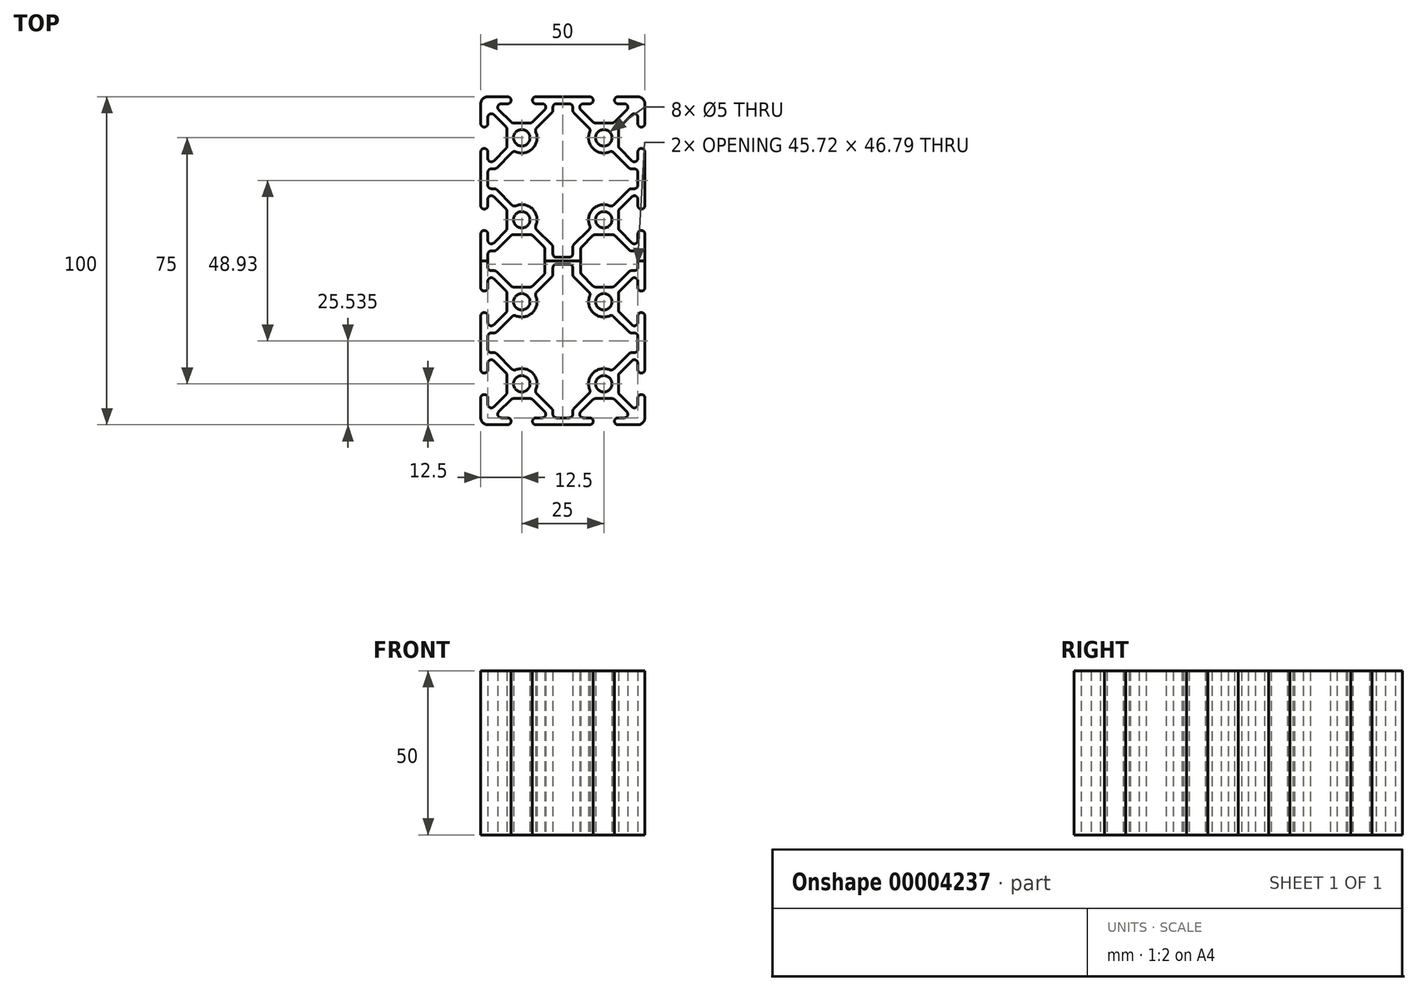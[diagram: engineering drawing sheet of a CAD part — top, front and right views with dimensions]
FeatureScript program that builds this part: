
annotation { "Feature Type Name" : "Feature", "Feature Type Description" : "" }
export const myFeature = defineFeature(function(context is Context, id is Id, definition is map)
    precondition{}
    {
        {
            var Q0;
            Q0=qCreatedBy(makeId("Top.planeOp"),FACE);
            var sketch = newSketch(context, id + "F0", { "sketchPlane" : qUnion([Q0])});
            skLineSegment(sketch, "E0", {"start": v(-12.5, 12.5) * mm, "end": v(-25, 25) * mm, "construction": true});
            skLineSegment(sketch, "E1", {"start": v(-25, 22.86) * mm, "end": v(-25, 16.82) * mm});
            skLineSegment(sketch, "E2", {"start": v(-22.86, 25) * mm, "end": v(-16.82, 25) * mm});
            skLineSegment(sketch, "E3", {"start": v(-16.82, 22.86) * mm, "end": v(-18.76, 22.86) * mm});
            skLineSegment(sketch, "E4", {"start": v(-22.86, 18.76) * mm, "end": v(-22.86, 16.82) * mm});
            skArc(sketch, "E5", {"start": v(-16.82, 25) * mm, "mid": v(-15.75, 23.93) * mm, "end": v(-16.82, 22.86) * mm});
            skArc(sketch, "E6", {"start": v(-22.86, 16.82) * mm, "mid": v(-23.93, 15.75) * mm, "end": v(-25, 16.82) * mm});
            skLineSegment(sketch, "E7", {"start": v(-19.52, 21.03) * mm, "end": v(-15.81, 17.32) * mm});
            skPoint(sketch, "E8.visualSharp", {"position": v(-25, 25) * mm});
            skLineSegment(sketch, "E8.filletArc", {"start": v(-25, 25) * mm, "end": v(-25, 25) * mm});
            skArc(sketch, "E9.filletArc", {"start": v(-21.03, 19.52) * mm, "mid": v(-22.2, 19.75) * mm, "end": v(-22.86, 18.76) * mm});
            skPoint(sketch, "E10.visualSharp", {"position": v(-21.35, 22.86) * mm});
            skArc(sketch, "E10.filletArc", {"start": v(-18.76, 22.86) * mm, "mid": v(-19.75, 22.2) * mm, "end": v(-19.52, 21.03) * mm});
            skArc(sketch, "E11.filletArc", {"start": v(-15.81, 17.32) * mm, "mid": v(-15.46, 17.1) * mm, "end": v(-15.05, 17.01) * mm});
            skCircle(sketch, "E12", {"center": v(-12.5, 12.5) * mm, "radius": 2.5 * mm});
            skLineSegment(sketch, "E13", {"start": v(0, 0) * mm, "end": v(0, 12.39) * mm, "construction": true});
            skCircle(sketch, "E14.0.MirrorC", {"center": v(12.5, 12.5) * mm, "radius": 2.5 * mm});
            skLineSegment(sketch, "E15", {"start": v(-12.5, 0) * mm, "end": v(-12.5, 12.5) * mm, "construction": true});
            skArc(sketch, "E16.0.MirrorCS", {"start": v(-9.19, 17.32) * mm, "mid": v(-9.54, 17.1) * mm, "end": v(-9.95, 17.01) * mm});
            skLineSegment(sketch, "E16.1.MirrorCS", {"start": v(-8.18, 22.86) * mm, "end": v(-6.24, 22.86) * mm});
            skLineSegment(sketch, "E16.3.MirrorCS", {"start": v(-5.48, 21.03) * mm, "end": v(-9.19, 17.32) * mm});
            skArc(sketch, "E16.8.MirrorCS", {"start": v(-8.18, 25) * mm, "mid": v(-9.25, 23.93) * mm, "end": v(-8.18, 22.86) * mm});
            skArc(sketch, "E16.11.MirrorCS", {"start": v(-6.24, 22.86) * mm, "mid": v(-5.25, 22.2) * mm, "end": v(-5.48, 21.03) * mm});
            skLineSegment(sketch, "E16.17.MirrorCS", {"start": v(0, 25) * mm, "end": v(-8.18, 25) * mm});
            skLineSegment(sketch, "E17", {"start": v(-15.05, 17.01) * mm, "end": v(-9.95, 17.01) * mm});
            skArc(sketch, "E18.1.MirrorCS", {"start": v(15.81, 17.32) * mm, "mid": v(15.46, 17.1) * mm, "end": v(15.05, 17.01) * mm});
            skArc(sketch, "E18.2.MirrorCS", {"start": v(9.19, 17.32) * mm, "mid": v(9.54, 17.1) * mm, "end": v(9.95, 17.01) * mm});
            skArc(sketch, "E18.3.MirrorCS", {"start": v(22.86, 16.82) * mm, "mid": v(23.93, 15.75) * mm, "end": v(25, 16.82) * mm});
            skLineSegment(sketch, "E18.5.MirrorCS", {"start": v(8.18, 22.86) * mm, "end": v(6.24, 22.86) * mm});
            skLineSegment(sketch, "E18.6.MirrorCS", {"start": v(19.52, 21.03) * mm, "end": v(15.81, 17.32) * mm});
            skLineSegment(sketch, "E18.7.MirrorCS", {"start": v(5.48, 21.03) * mm, "end": v(9.19, 17.32) * mm});
            skLineSegment(sketch, "E18.8.MirrorCS", {"start": v(12.5, 12.5) * mm, "end": v(25, 25) * mm, "construction": true});
            skArc(sketch, "E18.10.MirrorCS", {"start": v(16.82, 25) * mm, "mid": v(15.75, 23.93) * mm, "end": v(16.82, 22.86) * mm});
            skLineSegment(sketch, "E18.11.MirrorCS", {"start": v(15.05, 17.01) * mm, "end": v(9.95, 17.01) * mm});
            skPoint(sketch, "E18.12.MirrorP", {"position": v(21.35, 22.86) * mm});
            skLineSegment(sketch, "E18.14.MirrorCS", {"start": v(22.86, 25) * mm, "end": v(16.82, 25) * mm});
            skArc(sketch, "E18.15.MirrorCS", {"start": v(21.03, 19.52) * mm, "mid": v(22.2, 19.75) * mm, "end": v(22.86, 18.76) * mm});
            skPoint(sketch, "E18.16.MirrorP", {"position": v(25, 25) * mm});
            skLineSegment(sketch, "E18.17.MirrorCS", {"start": v(25, 22.86) * mm, "end": v(25, 16.82) * mm});
            skArc(sketch, "E18.18.MirrorCS", {"start": v(6.24, 22.86) * mm, "mid": v(5.25, 22.2) * mm, "end": v(5.48, 21.03) * mm});
            skArc(sketch, "E18.20.MirrorCS", {"start": v(18.76, 22.86) * mm, "mid": v(19.75, 22.2) * mm, "end": v(19.52, 21.03) * mm});
            skArc(sketch, "E18.21.MirrorCS", {"start": v(8.18, 25) * mm, "mid": v(9.25, 23.93) * mm, "end": v(8.18, 22.86) * mm});
            skLineSegment(sketch, "E18.22.MirrorCS", {"start": v(25, 25) * mm, "end": v(25, 25) * mm});
            skLineSegment(sketch, "E18.24.MirrorCS", {"start": v(22.86, 18.76) * mm, "end": v(22.86, 16.82) * mm});
            skLineSegment(sketch, "E18.25.MirrorCS", {"start": v(16.82, 22.86) * mm, "end": v(18.76, 22.86) * mm});
            skLineSegment(sketch, "E18.26.MirrorCS", {"start": v(0, 25) * mm, "end": v(8.18, 25) * mm});
            skLineSegment(sketch, "E19", {"start": v(-21.03, 19.52) * mm, "end": v(-17.32, 15.81) * mm});
            skLineSegment(sketch, "E20", {"start": v(0, 0) * mm, "end": v(-29.45, 0) * mm, "construction": true});
            skLineSegment(sketch, "E21", {"start": v(-17, 15.05) * mm, "end": v(-17, 12.5) * mm});
            skLineSegment(sketch, "E22", {"start": v(-12.5, 12.5) * mm, "end": v(-25, 12.5) * mm, "construction": true});
            skLineSegment(sketch, "E23.0.MirrorCS", {"start": v(21.03, 19.52) * mm, "end": v(17.32, 15.81) * mm});
            skLineSegment(sketch, "E24.0.MirrorCS", {"start": v(17, 15.05) * mm, "end": v(17, 12.5) * mm});
            skLineSegment(sketch, "E25.0.MirrorCS", {"start": v(-17, 9.95) * mm, "end": v(-17, 12.5) * mm});
            skLineSegment(sketch, "E26.0.MirrorCS", {"start": v(-21.03, 5.48) * mm, "end": v(-17.32, 9.19) * mm});
            skArc(sketch, "E27.0.MirrorCS", {"start": v(-21.03, 5.48) * mm, "mid": v(-22.2, 5.25) * mm, "end": v(-22.86, 6.24) * mm});
            skLineSegment(sketch, "E28.0.MirrorCS", {"start": v(-22.86, 6.24) * mm, "end": v(-22.86, 8.18) * mm});
            skArc(sketch, "E29.0.MirrorCS", {"start": v(-22.86, 8.18) * mm, "mid": v(-23.93, 9.25) * mm, "end": v(-25, 8.18) * mm});
            skLineSegment(sketch, "E30.0.MirrorCS", {"start": v(-25, 0) * mm, "end": v(-25, 8.18) * mm});
            skLineSegment(sketch, "E31.0.MirrorCS", {"start": v(17, 9.95) * mm, "end": v(17, 12.5) * mm});
            skLineSegment(sketch, "E32.0.MirrorCS", {"start": v(21.03, 5.48) * mm, "end": v(17.32, 9.19) * mm});
            skArc(sketch, "E33.0.MirrorCS", {"start": v(21.03, 5.48) * mm, "mid": v(22.2, 5.25) * mm, "end": v(22.86, 6.24) * mm});
            skLineSegment(sketch, "E34.0.MirrorCS", {"start": v(22.86, 6.24) * mm, "end": v(22.86, 8.18) * mm});
            skArc(sketch, "E35.0.MirrorCS", {"start": v(22.86, 8.18) * mm, "mid": v(23.93, 9.25) * mm, "end": v(25, 8.18) * mm});
            skLineSegment(sketch, "E36.0.MirrorCS", {"start": v(25, 0) * mm, "end": v(25, 8.18) * mm});
            skPoint(sketch, "E37.visualSharp", {"position": v(-17, 15.5) * mm});
            skArc(sketch, "E37.filletArc", {"start": v(-17, 15.05) * mm, "mid": v(-17.1, 15.46) * mm, "end": v(-17.32, 15.81) * mm});
            skPoint(sketch, "E38.visualSharp", {"position": v(-17, 9.5) * mm});
            skArc(sketch, "E38.filletArc", {"start": v(-17.32, 9.19) * mm, "mid": v(-17.1, 9.54) * mm, "end": v(-17, 9.95) * mm});
            skPoint(sketch, "E39.visualSharp", {"position": v(17, 9.5) * mm});
            skArc(sketch, "E39.filletArc", {"start": v(17, 9.95) * mm, "mid": v(17.1, 9.54) * mm, "end": v(17.32, 9.19) * mm});
            skPoint(sketch, "E40.visualSharp", {"position": v(17, 15.5) * mm});
            skArc(sketch, "E40.filletArc", {"start": v(17.32, 15.81) * mm, "mid": v(17.1, 15.46) * mm, "end": v(17, 15.05) * mm});
            skArc(sketch, "E41.1.MirrorCS", {"start": v(-17.32, -9.19) * mm, "mid": v(-17.1, -9.54) * mm, "end": v(-17, -9.95) * mm});
            skLineSegment(sketch, "E41.5.MirrorCS", {"start": v(-22.86, -6.24) * mm, "end": v(-22.86, -8.18) * mm});
            skLineSegment(sketch, "E41.8.MirrorCS", {"start": v(-12.5, 0) * mm, "end": v(-12.5, -12.5) * mm, "construction": true});
            skCircle(sketch, "E41.10.MirrorC", {"center": v(-12.5, -12.5) * mm, "radius": 2.5 * mm});
            skArc(sketch, "E41.12.MirrorCS", {"start": v(-21.03, -5.48) * mm, "mid": v(-22.2, -5.25) * mm, "end": v(-22.86, -6.24) * mm});
            skPoint(sketch, "E41.14.MirrorP", {"position": v(-17, -9.5) * mm});
            skLineSegment(sketch, "E41.15.MirrorCS", {"start": v(-21.03, -5.48) * mm, "end": v(-17.32, -9.19) * mm});
            skLineSegment(sketch, "E41.18.MirrorCS", {"start": v(-25, 0) * mm, "end": v(-25, -8.18) * mm});
            skArc(sketch, "E41.24.MirrorCS", {"start": v(-22.86, -8.18) * mm, "mid": v(-23.93, -9.25) * mm, "end": v(-25, -8.18) * mm});
            skLineSegment(sketch, "E41.29.MirrorCS", {"start": v(-12.5, -12.5) * mm, "end": v(-25, -12.5) * mm, "construction": true});
            skLineSegment(sketch, "E41.30.MirrorCS", {"start": v(-17, -9.95) * mm, "end": v(-17, -12.5) * mm});
            skArc(sketch, "E42.1.MirrorCS", {"start": v(17, -9.95) * mm, "mid": v(17.1, -9.54) * mm, "end": v(17.32, -9.19) * mm});
            skLineSegment(sketch, "E42.3.MirrorCS", {"start": v(22.86, -6.24) * mm, "end": v(22.86, -8.18) * mm});
            skArc(sketch, "E42.10.MirrorCS", {"start": v(21.03, -5.48) * mm, "mid": v(22.2, -5.25) * mm, "end": v(22.86, -6.24) * mm});
            skLineSegment(sketch, "E42.16.MirrorCS", {"start": v(17, -9.95) * mm, "end": v(17, -12.5) * mm});
            skArc(sketch, "E42.22.MirrorCS", {"start": v(22.86, -8.18) * mm, "mid": v(23.93, -9.25) * mm, "end": v(25, -8.18) * mm});
            skPoint(sketch, "E42.24.MirrorP", {"position": v(17, -9.5) * mm});
            skLineSegment(sketch, "E42.25.MirrorCS", {"start": v(21.03, -5.48) * mm, "end": v(17.32, -9.19) * mm});
            skCircle(sketch, "E42.27.MirrorC", {"center": v(12.5, -12.5) * mm, "radius": 2.5 * mm});
            skLineSegment(sketch, "E42.30.MirrorCS", {"start": v(25, 0) * mm, "end": v(25, -8.18) * mm});
            skArc(sketch, "E43.filletArc", {"start": v(-22.86, 25) * mm, "mid": v(-24.37, 24.37) * mm, "end": v(-25, 22.86) * mm});
            skArc(sketch, "E44.filletArc", {"start": v(25, 22.86) * mm, "mid": v(24.37, 24.37) * mm, "end": v(22.86, 25) * mm});
            skLineSegment(sketch, "E45", {"start": v(0, 22.86) * mm, "end": v(1.96, 22.86) * mm});
            skLineSegment(sketch, "E46", {"start": v(3.03, 21.8) * mm, "end": v(3.03, 20.9) * mm});
            skArc(sketch, "E47.0", {"start": v(14.31, 8.23) * mm, "mid": v(9.22, 9.22) * mm, "end": v(8.23, 14.31) * mm});
            skLineSegment(sketch, "E48.0", {"start": v(3.34, 20.15) * mm, "end": v(8, 15.49) * mm});
            skPoint(sketch, "E49.visualSharp", {"position": v(3.03, 22.86) * mm});
            skArc(sketch, "E49.filletArc", {"start": v(3.03, 21.8) * mm, "mid": v(2.71, 22.55) * mm, "end": v(1.96, 22.86) * mm});
            skPoint(sketch, "E50.visualSharp", {"position": v(8.55, 14.94) * mm});
            skArc(sketch, "E50.filletArc", {"start": v(8.23, 14.31) * mm, "mid": v(8.3, 14.93) * mm, "end": v(8, 15.49) * mm});
            skArc(sketch, "E51.0.MirrorCS", {"start": v(-14.31, 8.23) * mm, "mid": v(-9.22, 9.22) * mm, "end": v(-8.23, 14.31) * mm});
            skArc(sketch, "E52.0.MirrorCS", {"start": v(-8.23, 14.31) * mm, "mid": v(-8.3, 14.93) * mm, "end": v(-8, 15.49) * mm});
            skArc(sketch, "E53.0.MirrorCS", {"start": v(-3.03, 21.8) * mm, "mid": v(-2.71, 22.55) * mm, "end": v(-1.96, 22.86) * mm});
            skLineSegment(sketch, "E54.0.MirrorCS", {"start": v(0, 22.86) * mm, "end": v(-1.96, 22.86) * mm});
            skPoint(sketch, "E55.visualSharp", {"position": v(3.03, 20.46) * mm});
            skArc(sketch, "E55.filletArc", {"start": v(3.03, 20.9) * mm, "mid": v(3.1, 20.5) * mm, "end": v(3.34, 20.15) * mm});
            skLineSegment(sketch, "E56.0.MirrorCS", {"start": v(-3.34, 20.15) * mm, "end": v(-8, 15.49) * mm});
            skArc(sketch, "E57.0.MirrorCS", {"start": v(-3.03, 20.9) * mm, "mid": v(-3.1, 20.5) * mm, "end": v(-3.34, 20.15) * mm});
            skLineSegment(sketch, "E58.0.MirrorCS", {"start": v(-3.03, 21.8) * mm, "end": v(-3.03, 20.9) * mm});
            skPoint(sketch, "E59.visualSharp", {"position": v(-12.5, 7.86) * mm});
            skPoint(sketch, "E60.visualSharp", {"position": v(-12.5, -7.86) * mm});
            skPoint(sketch, "E61.visualSharp", {"position": v(12.5, -7.86) * mm});
            skArc(sketch, "E62.0.MirrorCS", {"start": v(-14.31, 8.23) * mm, "mid": v(-14.93, 8.3) * mm, "end": v(-15.49, 8) * mm});
            skLineSegment(sketch, "E63.0.MirrorCS", {"start": v(-20.15, 3.34) * mm, "end": v(-15.49, 8) * mm});
            skArc(sketch, "E64.0.MirrorCS", {"start": v(-20.9, 3.03) * mm, "mid": v(-20.5, 3.1) * mm, "end": v(-20.15, 3.34) * mm});
            skLineSegment(sketch, "E65.0.MirrorCS", {"start": v(-21.79, 3.03) * mm, "end": v(-20.9, 3.03) * mm});
            skArc(sketch, "E66.0.MirrorCS", {"start": v(-21.79, 3.03) * mm, "mid": v(-22.55, 2.71) * mm, "end": v(-22.86, 1.96) * mm});
            skLineSegment(sketch, "E67.0.MirrorCS", {"start": v(-22.86, 0) * mm, "end": v(-22.86, 1.96) * mm});
            skArc(sketch, "E68.0.MirrorCS", {"start": v(14.31, 8.23) * mm, "mid": v(14.93, 8.3) * mm, "end": v(15.49, 8) * mm});
            skArc(sketch, "E69.0.MirrorCS", {"start": v(-12.5, 7.86) * mm, "mid": v(-8.63, 9.94) * mm, "end": v(-8.23, 14.31) * mm});
            skLineSegment(sketch, "E70.0.MirrorCS", {"start": v(20.15, 3.34) * mm, "end": v(15.49, 8) * mm});
            skArc(sketch, "E71.0.MirrorCS", {"start": v(20.9, 3.03) * mm, "mid": v(20.5, 3.1) * mm, "end": v(20.15, 3.34) * mm});
            skLineSegment(sketch, "E72.0.MirrorCS", {"start": v(21.79, 3.03) * mm, "end": v(20.9, 3.03) * mm});
            skArc(sketch, "E73.0.MirrorCS", {"start": v(21.79, 3.03) * mm, "mid": v(22.55, 2.71) * mm, "end": v(22.86, 1.96) * mm});
            skLineSegment(sketch, "E74.0.MirrorCS", {"start": v(22.86, 0) * mm, "end": v(22.86, 1.96) * mm});
            skPoint(sketch, "E75.orphan", {"position": v(12.5, 7.86) * mm});
            skArc(sketch, "E76.0.MirrorCS", {"start": v(-20.9, -3.03) * mm, "mid": v(-20.5, -3.1) * mm, "end": v(-20.15, -3.34) * mm});
            skLineSegment(sketch, "E76.1.MirrorCS", {"start": v(-21.79, -3.03) * mm, "end": v(-20.9, -3.03) * mm});
            skArc(sketch, "E76.2.MirrorCS", {"start": v(-21.79, -3.03) * mm, "mid": v(-22.55, -2.71) * mm, "end": v(-22.86, -1.96) * mm});
            skLineSegment(sketch, "E76.3.MirrorCS", {"start": v(-22.86, 0) * mm, "end": v(-22.86, -1.96) * mm});
            skLineSegment(sketch, "E77.0.MirrorCS", {"start": v(-20.15, -3.34) * mm, "end": v(-15.49, -8) * mm});
            skArc(sketch, "E78.0.MirrorCS", {"start": v(-14.31, -8.23) * mm, "mid": v(-14.93, -8.3) * mm, "end": v(-15.49, -8) * mm});
            skArc(sketch, "E79.0.MirrorCS", {"start": v(-14.31, -8.23) * mm, "mid": v(-9.22, -9.22) * mm, "end": v(-8.23, -14.31) * mm});
            skArc(sketch, "E80.0.MirrorCS", {"start": v(14.31, -8.23) * mm, "mid": v(9.22, -9.22) * mm, "end": v(8.23, -14.31) * mm});
            skArc(sketch, "E81.0.MirrorCS", {"start": v(14.31, -8.23) * mm, "mid": v(14.93, -8.3) * mm, "end": v(15.49, -8) * mm});
            skLineSegment(sketch, "E82.0.MirrorCS", {"start": v(20.15, -3.34) * mm, "end": v(15.49, -8) * mm});
            skArc(sketch, "E83.0.MirrorCS", {"start": v(20.9, -3.03) * mm, "mid": v(20.5, -3.1) * mm, "end": v(20.15, -3.34) * mm});
            skLineSegment(sketch, "E84.0.MirrorCS", {"start": v(21.79, -3.03) * mm, "end": v(20.9, -3.03) * mm});
            skArc(sketch, "E85.0.MirrorCS", {"start": v(21.79, -3.03) * mm, "mid": v(22.55, -2.71) * mm, "end": v(22.86, -1.96) * mm});
            skLineSegment(sketch, "E86.0.MirrorCS", {"start": v(22.86, 0) * mm, "end": v(22.86, -1.96) * mm});
            skArc(sketch, "E87.1.MirrorCS", {"start": v(14.31, -33.23) * mm, "mid": v(14.93, -33.3) * mm, "end": v(15.49, -33) * mm});
            skLineSegment(sketch, "E87.2.MirrorCS", {"start": v(22.86, -25) * mm, "end": v(22.86, -23.04) * mm});
            skLineSegment(sketch, "E87.3.MirrorCS", {"start": v(21.79, -28.03) * mm, "end": v(20.9, -28.03) * mm});
            skLineSegment(sketch, "E87.4.MirrorCS", {"start": v(-22.86, -25) * mm, "end": v(-22.86, -23.04) * mm});
            skArc(sketch, "E87.5.MirrorCS", {"start": v(20.9, -28.03) * mm, "mid": v(20.5, -28.1) * mm, "end": v(20.15, -28.34) * mm});
            skArc(sketch, "E87.6.MirrorCS", {"start": v(21.79, -21.97) * mm, "mid": v(22.55, -22.29) * mm, "end": v(22.86, -23.04) * mm});
            skArc(sketch, "E87.7.MirrorCS", {"start": v(-21.79, -28.03) * mm, "mid": v(-22.55, -27.71) * mm, "end": v(-22.86, -26.96) * mm});
            skLineSegment(sketch, "E87.8.MirrorCS", {"start": v(-22.86, -18.76) * mm, "end": v(-22.86, -16.82) * mm});
            skArc(sketch, "E87.10.MirrorCS", {"start": v(-21.79, -21.97) * mm, "mid": v(-22.55, -22.29) * mm, "end": v(-22.86, -23.04) * mm});
            skLineSegment(sketch, "E87.12.MirrorCS", {"start": v(-21.79, -28.03) * mm, "end": v(-20.9, -28.03) * mm});
            skLineSegment(sketch, "E87.14.MirrorCS", {"start": v(-22.86, -31.24) * mm, "end": v(-22.86, -33.18) * mm});
            skArc(sketch, "E87.15.MirrorCS", {"start": v(17, -15.05) * mm, "mid": v(17.1, -15.46) * mm, "end": v(17.32, -15.81) * mm});
            skArc(sketch, "E87.16.MirrorCS", {"start": v(17, -34.95) * mm, "mid": v(17.1, -34.54) * mm, "end": v(17.32, -34.19) * mm});
            skLineSegment(sketch, "E87.17.MirrorCS", {"start": v(22.86, -25) * mm, "end": v(22.86, -26.96) * mm});
            skArc(sketch, "E87.18.MirrorCS", {"start": v(-20.9, -28.03) * mm, "mid": v(-20.5, -28.1) * mm, "end": v(-20.15, -28.34) * mm});
            skLineSegment(sketch, "E87.19.MirrorCS", {"start": v(22.86, -18.76) * mm, "end": v(22.86, -16.82) * mm});
            skArc(sketch, "E87.20.MirrorCS", {"start": v(20.9, -21.97) * mm, "mid": v(20.5, -21.9) * mm, "end": v(20.15, -21.66) * mm});
            skArc(sketch, "E87.21.MirrorCS", {"start": v(-17.32, -34.19) * mm, "mid": v(-17.1, -34.54) * mm, "end": v(-17.01, -34.95) * mm});
            skLineSegment(sketch, "E87.22.MirrorCS", {"start": v(22.86, -31.24) * mm, "end": v(22.86, -33.18) * mm});
            skLineSegment(sketch, "E87.23.MirrorCS", {"start": v(-22.86, -25) * mm, "end": v(-22.86, -26.96) * mm});
            skArc(sketch, "E87.24.MirrorCS", {"start": v(-20.9, -21.97) * mm, "mid": v(-20.5, -21.9) * mm, "end": v(-20.15, -21.66) * mm});
            skLineSegment(sketch, "E87.25.MirrorCS", {"start": v(21.79, -21.97) * mm, "end": v(20.9, -21.97) * mm});
            skLineSegment(sketch, "E87.26.MirrorCS", {"start": v(-21.79, -21.97) * mm, "end": v(-20.9, -21.97) * mm});
            skArc(sketch, "E87.27.MirrorCS", {"start": v(21.79, -28.03) * mm, "mid": v(22.55, -27.71) * mm, "end": v(22.86, -26.96) * mm});
            skArc(sketch, "E87.28.MirrorCS", {"start": v(-17.32, -15.81) * mm, "mid": v(-17.1, -15.46) * mm, "end": v(-17, -15.05) * mm});
            skLineSegment(sketch, "E87.29.MirrorCS", {"start": v(-25, -25) * mm, "end": v(-25, -33.18) * mm});
            skLineSegment(sketch, "E87.30.MirrorCS", {"start": v(17.01, -9.95) * mm, "end": v(17.01, -12.5) * mm});
            skLineSegment(sketch, "E87.31.MirrorCS", {"start": v(21.03, -19.52) * mm, "end": v(17.32, -15.81) * mm});
            skLineSegment(sketch, "E87.32.MirrorCS", {"start": v(-20.15, -28.34) * mm, "end": v(-15.81, -32.68) * mm});
            skPoint(sketch, "E87.33.MirrorP", {"position": v(-17, -15.5) * mm});
            skArc(sketch, "E87.35.MirrorCS", {"start": v(-22.86, -16.82) * mm, "mid": v(-23.93, -15.75) * mm, "end": v(-25, -16.82) * mm});
            skLineSegment(sketch, "E87.36.MirrorCS", {"start": v(-21.03, -30.48) * mm, "end": v(-17.32, -34.19) * mm});
            skLineSegment(sketch, "E87.37.MirrorCS", {"start": v(20.15, -21.66) * mm, "end": v(15.81, -17.32) * mm});
            skArc(sketch, "E87.38.MirrorCS", {"start": v(-21.03, -19.52) * mm, "mid": v(-22.2, -19.75) * mm, "end": v(-22.86, -18.76) * mm});
            skArc(sketch, "E87.39.MirrorCS", {"start": v(-22.86, -33.18) * mm, "mid": v(-23.93, -34.25) * mm, "end": v(-25, -33.18) * mm});
            skLineSegment(sketch, "E87.41.MirrorCS", {"start": v(0, -25) * mm, "end": v(-29.45, -25) * mm, "construction": true});
            skLineSegment(sketch, "E87.42.MirrorCS", {"start": v(-17, -15.05) * mm, "end": v(-17, -12.5) * mm});
            skArc(sketch, "E87.43.MirrorCS", {"start": v(22.86, -33.18) * mm, "mid": v(23.93, -34.25) * mm, "end": v(25, -33.18) * mm});
            skLineSegment(sketch, "E87.44.MirrorCS", {"start": v(17, -15.05) * mm, "end": v(17, -12.5) * mm});
            skLineSegment(sketch, "E87.46.MirrorCS", {"start": v(21.03, -30.48) * mm, "end": v(17.32, -34.19) * mm});
            skPoint(sketch, "E87.48.MirrorP", {"position": v(17, -15.5) * mm});
            skPoint(sketch, "E87.49.MirrorP", {"position": v(-17.01, -34.5) * mm});
            skPoint(sketch, "E87.50.MirrorP", {"position": v(-12.5, -17.14) * mm});
            skLineSegment(sketch, "E87.51.MirrorCS", {"start": v(25, -25) * mm, "end": v(25, -33.18) * mm});
            skLineSegment(sketch, "E87.52.MirrorCS", {"start": v(25, -25) * mm, "end": v(25, -16.82) * mm});
            skLineSegment(sketch, "E87.53.MirrorCS", {"start": v(17, -34.95) * mm, "end": v(17, -37.5) * mm});
            skArc(sketch, "E87.54.MirrorCS", {"start": v(21.03, -30.48) * mm, "mid": v(22.2, -30.25) * mm, "end": v(22.86, -31.24) * mm});
            skLineSegment(sketch, "E87.55.MirrorCS", {"start": v(-25, -25) * mm, "end": v(-25, -16.82) * mm});
            skLineSegment(sketch, "E87.57.MirrorCS", {"start": v(-20.15, -21.66) * mm, "end": v(-15.81, -17.32) * mm});
            skPoint(sketch, "E87.58.MirrorP", {"position": v(12.5, -32.86) * mm});
            skPoint(sketch, "E87.59.MirrorP", {"position": v(17, -34.5) * mm});
            skLineSegment(sketch, "E87.60.MirrorCS", {"start": v(-12.5, -37.5) * mm, "end": v(-25, -37.5) * mm, "construction": true});
            skArc(sketch, "E87.61.MirrorCS", {"start": v(21.03, -19.52) * mm, "mid": v(22.2, -19.75) * mm, "end": v(22.86, -18.76) * mm});
            skLineSegment(sketch, "E87.62.MirrorCS", {"start": v(0, -25) * mm, "end": v(0, -37.39) * mm, "construction": true});
            skLineSegment(sketch, "E87.64.MirrorCS", {"start": v(20.15, -28.34) * mm, "end": v(15.81, -32.68) * mm});
            skArc(sketch, "E87.65.MirrorCS", {"start": v(22.86, -16.82) * mm, "mid": v(23.93, -15.75) * mm, "end": v(25, -16.82) * mm});
            skLineSegment(sketch, "E87.66.MirrorCS", {"start": v(-17.01, -34.95) * mm, "end": v(-17.01, -37.5) * mm});
            skLineSegment(sketch, "E87.67.MirrorCS", {"start": v(-12.5, -25) * mm, "end": v(-12.5, -37.5) * mm, "construction": true});
            skArc(sketch, "E87.68.MirrorCS", {"start": v(-21.03, -30.48) * mm, "mid": v(-22.2, -30.25) * mm, "end": v(-22.86, -31.24) * mm});
            skLineSegment(sketch, "E87.69.MirrorCS", {"start": v(-12.5, -25) * mm, "end": v(-12.5, -12.5) * mm, "construction": true});
            skLineSegment(sketch, "E87.70.MirrorCS", {"start": v(-21.03, -19.52) * mm, "end": v(-17.32, -15.81) * mm});
            skLineSegment(sketch, "E88.0.MirrorCS", {"start": v(-3.34, -20.15) * mm, "end": v(-8, -15.49) * mm});
            skLineSegment(sketch, "E89.0.MirrorCS", {"start": v(-5.8, -20.72) * mm, "end": v(-9.19, -17.32) * mm});
            skArc(sketch, "E90.0.MirrorCS", {"start": v(-3.03, -20.9) * mm, "mid": v(-3.1, -20.5) * mm, "end": v(-3.34, -20.15) * mm});
            skLineSegment(sketch, "E91.0.MirrorCS", {"start": v(-3.03, -22.86) * mm, "end": v(-3.03, -20.9) * mm});
            skLineSegment(sketch, "E92.0.MirrorCS", {"start": v(3.34, -20.15) * mm, "end": v(8, -15.49) * mm});
            skArc(sketch, "E93.0.MirrorCS", {"start": v(3.03, -20.9) * mm, "mid": v(3.1, -20.5) * mm, "end": v(3.34, -20.15) * mm});
            skLineSegment(sketch, "E94.0.MirrorCS", {"start": v(3.03, -22.86) * mm, "end": v(3.03, -20.9) * mm});
            skPoint(sketch, "E95.newPointA", {"position": v(-8.23, -14.31) * mm});
            skPoint(sketch, "E95.newPointB", {"position": v(-8, -15.49) * mm});
            skArc(sketch, "E95.filletArc", {"start": v(-8.23, -14.31) * mm, "mid": v(-8.3, -14.93) * mm, "end": v(-8, -15.49) * mm});
            skPoint(sketch, "E96.newPointA", {"position": v(8.23, -14.31) * mm});
            skPoint(sketch, "E96.newPointB", {"position": v(8, -15.49) * mm});
            skArc(sketch, "E96.filletArc", {"start": v(8, -15.49) * mm, "mid": v(8.3, -14.93) * mm, "end": v(8.23, -14.31) * mm});
            skLineSegment(sketch, "E97.0.MirrorCS", {"start": v(-15.05, -17.01) * mm, "end": v(-9.95, -17.01) * mm});
            skPoint(sketch, "E98.newPointB", {"position": v(-15.05, -17.01) * mm});
            skArc(sketch, "E98.filletArc", {"start": v(-15.05, -17.01) * mm, "mid": v(-15.46, -17.1) * mm, "end": v(-15.81, -17.32) * mm});
            skPoint(sketch, "E99.visualSharp", {"position": v(-9.5, -17) * mm});
            skArc(sketch, "E99.filletArc", {"start": v(-9.19, -17.32) * mm, "mid": v(-9.54, -17.1) * mm, "end": v(-9.95, -17.01) * mm});
            skLineSegment(sketch, "E100.0.MirrorCS", {"start": v(-15.05, -32.99) * mm, "end": v(-9.95, -32.99) * mm});
            skLineSegment(sketch, "E101.0.MirrorCS", {"start": v(-5.8, -29.28) * mm, "end": v(-9.19, -32.68) * mm});
            skPoint(sketch, "E102.newPointB", {"position": v(-15.05, -32.99) * mm});
            skArc(sketch, "E102.filletArc", {"start": v(-15.81, -32.68) * mm, "mid": v(-15.46, -32.9) * mm, "end": v(-15.05, -32.99) * mm});
            skPoint(sketch, "E103.newPointA", {"position": v(-9.19, -32.68) * mm});
            skPoint(sketch, "E103.newPointB", {"position": v(-9.95, -32.99) * mm});
            skArc(sketch, "E103.filletArc", {"start": v(-9.95, -32.99) * mm, "mid": v(-9.54, -32.9) * mm, "end": v(-9.19, -32.68) * mm});
            skLineSegment(sketch, "E104", {"start": v(-5.48, -21.48) * mm, "end": v(-5.48, -28.52) * mm});
            skPoint(sketch, "E105.visualSharp", {"position": v(-5.48, -21.03) * mm});
            skArc(sketch, "E105.filletArc", {"start": v(-5.48, -21.48) * mm, "mid": v(-5.56, -21.07) * mm, "end": v(-5.8, -20.72) * mm});
            skPoint(sketch, "E106.visualSharp", {"position": v(-5.48, -28.97) * mm});
            skArc(sketch, "E106.filletArc", {"start": v(-5.8, -29.28) * mm, "mid": v(-5.56, -28.93) * mm, "end": v(-5.48, -28.52) * mm});
            skLineSegment(sketch, "E107", {"start": v(-1.96, -23.93) * mm, "end": v(1.96, -23.93) * mm});
            skPoint(sketch, "E108.orphan", {"position": v(-3.03, -21.8) * mm});
            skPoint(sketch, "E109.orphan", {"position": v(3.03, -21.8) * mm});
            skArc(sketch, "E110.filletArc", {"start": v(-3.03, -22.86) * mm, "mid": v(-2.71, -23.62) * mm, "end": v(-1.96, -23.93) * mm});
            skArc(sketch, "E111.filletArc", {"start": v(1.96, -23.93) * mm, "mid": v(2.71, -23.62) * mm, "end": v(3.03, -22.86) * mm});
            skLineSegment(sketch, "E112.0.MirrorCS", {"start": v(15.05, -17.01) * mm, "end": v(9.95, -17.01) * mm});
            skLineSegment(sketch, "E113.0.MirrorCS", {"start": v(5.8, -20.72) * mm, "end": v(9.19, -17.32) * mm});
            skLineSegment(sketch, "E114.0.MirrorCS", {"start": v(5.48, -21.48) * mm, "end": v(5.48, -28.52) * mm});
            skLineSegment(sketch, "E115.0.MirrorCS", {"start": v(5.8, -29.28) * mm, "end": v(9.19, -32.68) * mm});
            skLineSegment(sketch, "E116.0.MirrorCS", {"start": v(15.05, -33) * mm, "end": v(9.95, -33) * mm});
            skPoint(sketch, "E117.newPointA", {"position": v(9.19, -17.32) * mm});
            skPoint(sketch, "E117.newPointB", {"position": v(9.95, -17.01) * mm});
            skArc(sketch, "E117.filletArc", {"start": v(9.95, -17.01) * mm, "mid": v(9.54, -17.1) * mm, "end": v(9.19, -17.32) * mm});
            skPoint(sketch, "E118.newPointA", {"position": v(15.05, -17.01) * mm});
            skArc(sketch, "E118.filletArc", {"start": v(15.81, -17.32) * mm, "mid": v(15.46, -17.1) * mm, "end": v(15.05, -17.01) * mm});
            skPoint(sketch, "E119.newPointA", {"position": v(15.05, -33) * mm});
            skPoint(sketch, "E119.newPointB", {"position": v(15.49, -33) * mm});
            skArc(sketch, "E119.filletArc", {"start": v(15.05, -33) * mm, "mid": v(15.46, -32.9) * mm, "end": v(15.81, -32.68) * mm});
            skPoint(sketch, "E120.newPointA", {"position": v(5.8, -29.28) * mm});
            skPoint(sketch, "E120.newPointB", {"position": v(5.48, -28.52) * mm});
            skArc(sketch, "E120.filletArc", {"start": v(5.48, -28.52) * mm, "mid": v(5.56, -28.93) * mm, "end": v(5.8, -29.28) * mm});
            skPoint(sketch, "E121.newPointA", {"position": v(9.19, -32.68) * mm});
            skPoint(sketch, "E121.newPointB", {"position": v(9.95, -33) * mm});
            skArc(sketch, "E121.filletArc", {"start": v(9.19, -32.68) * mm, "mid": v(9.54, -32.9) * mm, "end": v(9.95, -33) * mm});
            skPoint(sketch, "E122.newPointA", {"position": v(5.8, -20.72) * mm});
            skPoint(sketch, "E122.newPointB", {"position": v(5.48, -21.48) * mm});
            skArc(sketch, "E122.filletArc", {"start": v(5.8, -20.72) * mm, "mid": v(5.56, -21.07) * mm, "end": v(5.48, -21.48) * mm});
            skLineSegment(sketch, "E123.0.MirrorCS", {"start": v(-17.01, -40.05) * mm, "end": v(-17.01, -37.5) * mm});
            skLineSegment(sketch, "E124", {"start": v(-25, -25) * mm, "end": v(25, -25) * mm});
            skSolve(sketch);
        }
        {
            var Q0;
            Q0=makeQuery(id+"F0.imprint","IMPRINT",FACE,{"disambiguationData":[TD([[makeQuery(id+"F0.imprint","IMPRINT",EDGE,{"derivedFrom":sQuery(id+"F0.wireOp",EDGE,"E1")}),1.0]])]});
            extrude(context, id + "F1", {"entities" : qUnion([Q0]), "depth" : 50 * mm});
        }
        {
            var Q0;
            Q0=makeQuery(id+"F1.opExtrude","SWEPT_BODY",BODY,{"disambiguationData":[OSD([sQuery(id+"F0.wireOp",EDGE,"E1"),sQuery(id+"F0.wireOp",EDGE,"E2"),sQuery(id+"F0.wireOp",EDGE,"E3"),sQuery(id+"F0.wireOp",EDGE,"E4"),sQuery(id+"F0.wireOp",EDGE,"E5"),sQuery(id+"F0.wireOp",EDGE,"E6"),sQuery(id+"F0.wireOp",EDGE,"E7"),sQuery(id+"F0.wireOp",EDGE,"E9.filletArc"),sQuery(id+"F0.wireOp",EDGE,"E10.filletArc"),sQuery(id+"F0.wireOp",EDGE,"E11.filletArc"),sQuery(id+"F0.wireOp",EDGE,"E12"),sQuery(id+"F0.wireOp",EDGE,"E14.0.MirrorC"),sQuery(id+"F0.wireOp",EDGE,"E16.0.MirrorCS"),sQuery(id+"F0.wireOp",EDGE,"E16.1.MirrorCS"),sQuery(id+"F0.wireOp",EDGE,"E16.3.MirrorCS"),sQuery(id+"F0.wireOp",EDGE,"E16.8.MirrorCS"),sQuery(id+"F0.wireOp",EDGE,"E16.11.MirrorCS"),sQuery(id+"F0.wireOp",EDGE,"E17"),sQuery(id+"F0.wireOp",EDGE,"E18.1.MirrorCS"),sQuery(id+"F0.wireOp",EDGE,"E18.2.MirrorCS"),sQuery(id+"F0.wireOp",EDGE,"E18.5.MirrorCS"),sQuery(id+"F0.wireOp",EDGE,"E18.6.MirrorCS"),sQuery(id+"F0.wireOp",EDGE,"E18.7.MirrorCS"),sQuery(id+"F0.wireOp",EDGE,"E18.10.MirrorCS"),sQuery(id+"F0.wireOp",EDGE,"E18.11.MirrorCS"),sQuery(id+"F0.wireOp",EDGE,"E18.14.MirrorCS"),sQuery(id+"F0.wireOp",EDGE,"E18.15.MirrorCS"),sQuery(id+"F0.wireOp",EDGE,"E18.17.MirrorCS"),sQuery(id+"F0.wireOp",EDGE,"E18.18.MirrorCS"),sQuery(id+"F0.wireOp",EDGE,"E18.20.MirrorCS"),sQuery(id+"F0.wireOp",EDGE,"E18.21.MirrorCS"),sQuery(id+"F0.wireOp",EDGE,"E18.24.MirrorCS"),sQuery(id+"F0.wireOp",EDGE,"E18.25.MirrorCS"),sQuery(id+"F0.wireOp",EDGE,"E18.26.MirrorCS"),sQuery(id+"F0.wireOp",EDGE,"E18.3.MirrorCS"),sQuery(id+"F0.wireOp",EDGE,"E19"),sQuery(id+"F0.wireOp",EDGE,"E21"),sQuery(id+"F0.wireOp",EDGE,"E23.0.MirrorCS"),sQuery(id+"F0.wireOp",EDGE,"E26.0.MirrorCS"),sQuery(id+"F0.wireOp",EDGE,"E27.0.MirrorCS"),sQuery(id+"F0.wireOp",EDGE,"E28.0.MirrorCS"),sQuery(id+"F0.wireOp",EDGE,"E29.0.MirrorCS"),sQuery(id+"F0.wireOp",EDGE,"E30.0.MirrorCS"),sQuery(id+"F0.wireOp",EDGE,"E31.0.MirrorCS"),sQuery(id+"F0.wireOp",EDGE,"E32.0.MirrorCS"),sQuery(id+"F0.wireOp",EDGE,"E33.0.MirrorCS"),sQuery(id+"F0.wireOp",EDGE,"E34.0.MirrorCS"),sQuery(id+"F0.wireOp",EDGE,"E35.0.MirrorCS"),sQuery(id+"F0.wireOp",EDGE,"E37.filletArc"),sQuery(id+"F0.wireOp",EDGE,"E38.filletArc"),sQuery(id+"F0.wireOp",EDGE,"E39.filletArc"),sQuery(id+"F0.wireOp",EDGE,"E40.filletArc"),sQuery(id+"F0.wireOp",EDGE,"E41.1.MirrorCS"),sQuery(id+"F0.wireOp",EDGE,"E41.5.MirrorCS"),sQuery(id+"F0.wireOp",EDGE,"E41.12.MirrorCS"),sQuery(id+"F0.wireOp",EDGE,"E41.15.MirrorCS"),sQuery(id+"F0.wireOp",EDGE,"E41.24.MirrorCS"),sQuery(id+"F0.wireOp",EDGE,"E42.1.MirrorCS"),sQuery(id+"F0.wireOp",EDGE,"E42.3.MirrorCS"),sQuery(id+"F0.wireOp",EDGE,"E42.10.MirrorCS"),sQuery(id+"F0.wireOp",EDGE,"E42.22.MirrorCS"),sQuery(id+"F0.wireOp",EDGE,"E42.25.MirrorCS"),sQuery(id+"F0.wireOp",EDGE,"E42.30.MirrorCS"),sQuery(id+"F0.wireOp",EDGE,"E43.filletArc"),sQuery(id+"F0.wireOp",EDGE,"E44.filletArc"),sQuery(id+"F0.wireOp",EDGE,"E45"),sQuery(id+"F0.wireOp",EDGE,"E46"),sQuery(id+"F0.wireOp",EDGE,"E47.0"),sQuery(id+"F0.wireOp",EDGE,"E48.0"),sQuery(id+"F0.wireOp",EDGE,"E49.filletArc"),sQuery(id+"F0.wireOp",EDGE,"E50.filletArc"),sQuery(id+"F0.wireOp",EDGE,"E51.0.MirrorCS"),sQuery(id+"F0.wireOp",EDGE,"E52.0.MirrorCS"),sQuery(id+"F0.wireOp",EDGE,"E53.0.MirrorCS"),sQuery(id+"F0.wireOp",EDGE,"E55.filletArc"),sQuery(id+"F0.wireOp",EDGE,"E56.0.MirrorCS"),sQuery(id+"F0.wireOp",EDGE,"E57.0.MirrorCS"),sQuery(id+"F0.wireOp",EDGE,"E58.0.MirrorCS"),sQuery(id+"F0.wireOp",EDGE,"E62.0.MirrorCS"),sQuery(id+"F0.wireOp",EDGE,"E63.0.MirrorCS"),sQuery(id+"F0.wireOp",EDGE,"E64.0.MirrorCS"),sQuery(id+"F0.wireOp",EDGE,"E65.0.MirrorCS"),sQuery(id+"F0.wireOp",EDGE,"E66.0.MirrorCS"),sQuery(id+"F0.wireOp",EDGE,"E67.0.MirrorCS"),sQuery(id+"F0.wireOp",EDGE,"E69.0.MirrorCS"),sQuery(id+"F0.wireOp",EDGE,"E68.0.MirrorCS"),sQuery(id+"F0.wireOp",EDGE,"E70.0.MirrorCS"),sQuery(id+"F0.wireOp",EDGE,"E71.0.MirrorCS"),sQuery(id+"F0.wireOp",EDGE,"E72.0.MirrorCS"),sQuery(id+"F0.wireOp",EDGE,"E73.0.MirrorCS"),sQuery(id+"F0.wireOp",EDGE,"E74.0.MirrorCS"),sQuery(id+"F0.wireOp",EDGE,"E76.0.MirrorCS"),sQuery(id+"F0.wireOp",EDGE,"E76.1.MirrorCS"),sQuery(id+"F0.wireOp",EDGE,"E76.2.MirrorCS"),sQuery(id+"F0.wireOp",EDGE,"E76.3.MirrorCS"),sQuery(id+"F0.wireOp",EDGE,"E77.0.MirrorCS"),sQuery(id+"F0.wireOp",EDGE,"E78.0.MirrorCS"),sQuery(id+"F0.wireOp",EDGE,"E79.0.MirrorCS"),sQuery(id+"F0.wireOp",EDGE,"E80.0.MirrorCS"),sQuery(id+"F0.wireOp",EDGE,"E81.0.MirrorCS"),sQuery(id+"F0.wireOp",EDGE,"E82.0.MirrorCS"),sQuery(id+"F0.wireOp",EDGE,"E83.0.MirrorCS"),sQuery(id+"F0.wireOp",EDGE,"E84.0.MirrorCS"),sQuery(id+"F0.wireOp",EDGE,"E85.0.MirrorCS"),sQuery(id+"F0.wireOp",EDGE,"E86.0.MirrorCS"),sQuery(id+"F0.wireOp",EDGE,"E87.2.MirrorCS"),sQuery(id+"F0.wireOp",EDGE,"E87.4.MirrorCS"),sQuery(id+"F0.wireOp",EDGE,"E87.6.MirrorCS"),sQuery(id+"F0.wireOp",EDGE,"E87.8.MirrorCS"),sQuery(id+"F0.wireOp",EDGE,"E87.10.MirrorCS"),sQuery(id+"F0.wireOp",EDGE,"E87.15.MirrorCS"),sQuery(id+"F0.wireOp",EDGE,"E87.19.MirrorCS"),sQuery(id+"F0.wireOp",EDGE,"E87.20.MirrorCS"),sQuery(id+"F0.wireOp",EDGE,"E87.24.MirrorCS"),sQuery(id+"F0.wireOp",EDGE,"E87.25.MirrorCS"),sQuery(id+"F0.wireOp",EDGE,"E87.26.MirrorCS"),sQuery(id+"F0.wireOp",EDGE,"E87.28.MirrorCS"),sQuery(id+"F0.wireOp",EDGE,"E87.31.MirrorCS"),sQuery(id+"F0.wireOp",EDGE,"E87.35.MirrorCS"),sQuery(id+"F0.wireOp",EDGE,"E87.37.MirrorCS"),sQuery(id+"F0.wireOp",EDGE,"E87.38.MirrorCS"),sQuery(id+"F0.wireOp",EDGE,"E87.44.MirrorCS"),sQuery(id+"F0.wireOp",EDGE,"E41.30.MirrorCS"),sQuery(id+"F0.wireOp",EDGE,"E87.52.MirrorCS"),sQuery(id+"F0.wireOp",EDGE,"E87.55.MirrorCS"),sQuery(id+"F0.wireOp",EDGE,"E41.10.MirrorC"),sQuery(id+"F0.wireOp",EDGE,"E87.57.MirrorCS"),sQuery(id+"F0.wireOp",EDGE,"E87.61.MirrorCS"),sQuery(id+"F0.wireOp",EDGE,"E87.65.MirrorCS"),sQuery(id+"F0.wireOp",EDGE,"E87.70.MirrorCS"),sQuery(id+"F0.wireOp",EDGE,"E42.27.MirrorC"),sQuery(id+"F0.wireOp",EDGE,"E88.0.MirrorCS"),sQuery(id+"F0.wireOp",EDGE,"E89.0.MirrorCS"),sQuery(id+"F0.wireOp",EDGE,"E90.0.MirrorCS"),sQuery(id+"F0.wireOp",EDGE,"E91.0.MirrorCS"),sQuery(id+"F0.wireOp",EDGE,"E92.0.MirrorCS"),sQuery(id+"F0.wireOp",EDGE,"E93.0.MirrorCS"),sQuery(id+"F0.wireOp",EDGE,"E94.0.MirrorCS"),sQuery(id+"F0.wireOp",EDGE,"E95.filletArc"),sQuery(id+"F0.wireOp",EDGE,"E96.filletArc"),sQuery(id+"F0.wireOp",EDGE,"E97.0.MirrorCS"),sQuery(id+"F0.wireOp",EDGE,"E98.filletArc"),sQuery(id+"F0.wireOp",EDGE,"E99.filletArc"),sQuery(id+"F0.wireOp",EDGE,"E104"),sQuery(id+"F0.wireOp",EDGE,"E105.filletArc"),sQuery(id+"F0.wireOp",EDGE,"E54.0.MirrorCS"),sQuery(id+"F0.wireOp",EDGE,"E107"),sQuery(id+"F0.wireOp",EDGE,"E110.filletArc"),sQuery(id+"F0.wireOp",EDGE,"E111.filletArc"),sQuery(id+"F0.wireOp",EDGE,"E112.0.MirrorCS"),sQuery(id+"F0.wireOp",EDGE,"E113.0.MirrorCS"),sQuery(id+"F0.wireOp",EDGE,"E114.0.MirrorCS"),sQuery(id+"F0.wireOp",EDGE,"E117.filletArc"),sQuery(id+"F0.wireOp",EDGE,"E118.filletArc"),sQuery(id+"F0.wireOp",EDGE,"E122.filletArc"),sQuery(id+"F0.wireOp",EDGE,"E124")])]});
            var Q1;
            {var subQ0=sQuery(id+"F0.wireOp",EDGE,"E124");Q1=makeQuery(id+"F1.opExtrude","SWEPT_FACE",FACE,{"disambiguationData":[OSD([subQ0]),TDD([makeQuery(id+"F0.imprint","IMPRINT",EDGE,{"disambiguationData":[TD([[makeQuery(id+"F0.imprint","INTERSECT",VERTEX,{"derivedFrom":[sQuery(id+"F0.wireOp",EDGE,"E104"),subQ0]}),-1.0]])],"derivedFrom":subQ0})])]});}
            mirror(context, id + "F2", {"entities" : qUnion([Q0]), "mirrorPlane" : qUnion([Q1])});
        }
    });
